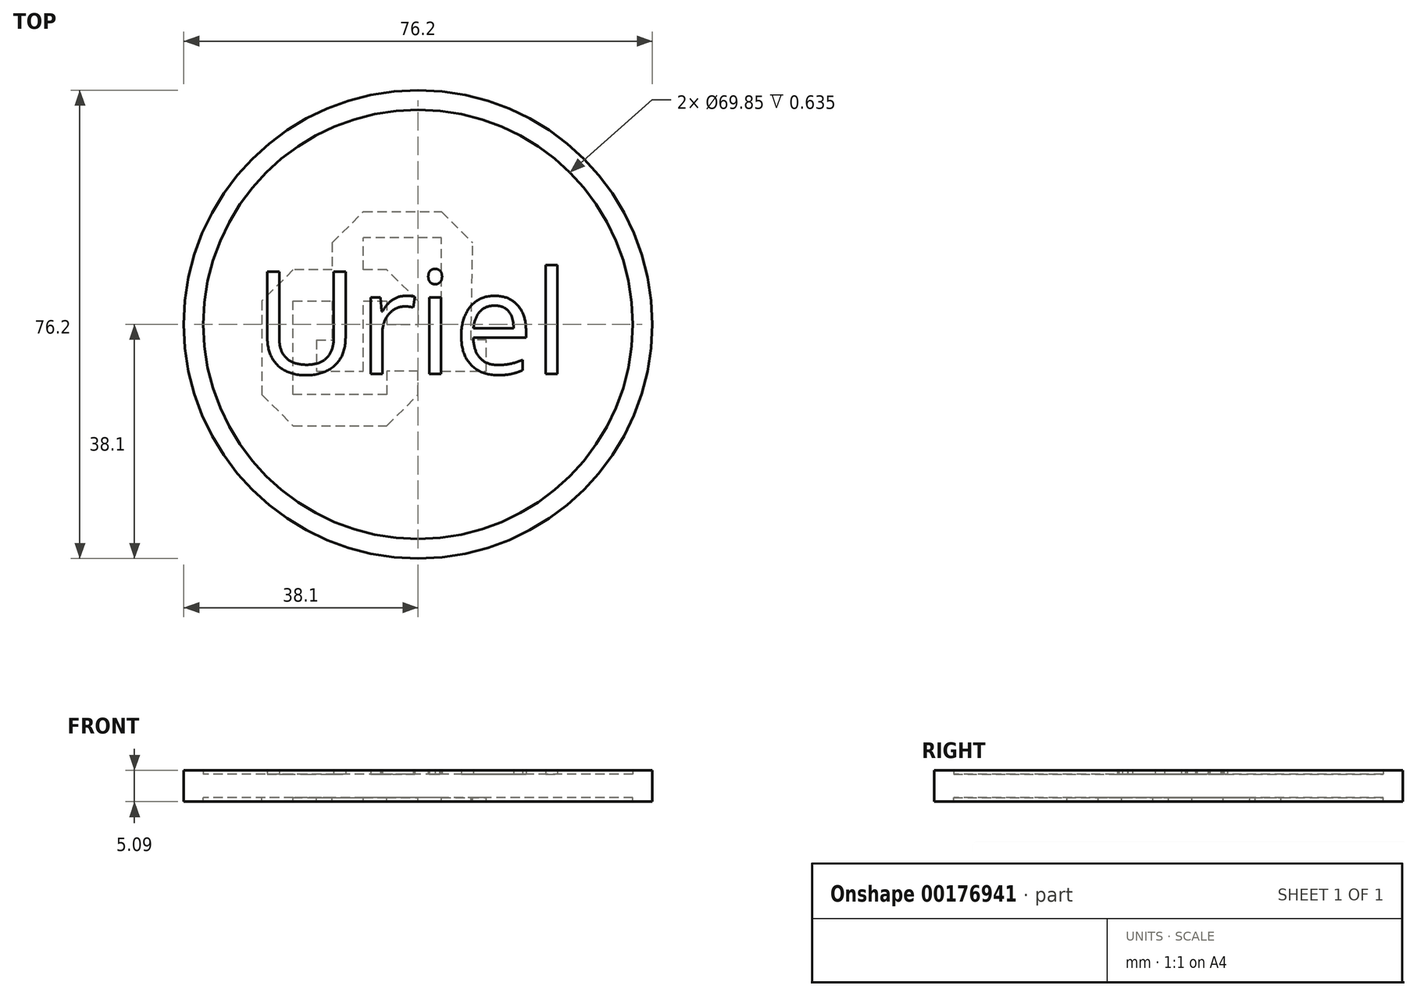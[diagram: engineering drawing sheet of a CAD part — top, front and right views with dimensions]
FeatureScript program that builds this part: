
annotation { "Feature Type Name" : "Feature", "Feature Type Description" : "" }
export const myFeature = defineFeature(function(context is Context, id is Id, definition is map)
    precondition{}
    {
        {
            var Q0;
            Q0=qCreatedBy(makeId("Top.planeOp"),FACE);
            var sketch = newSketch(context, id + "F0", { "sketchPlane" : qUnion([Q0])});
            skCircle(sketch, "E0", {"center": v(0, 0) * mm, "radius": 38.1 * mm});
            skSolve(sketch);
        }
        {
            var Q0;
            Q0 = qSketchRegion(id + "F0", true);
            extrude(context, id + "F1", {"entities" : qUnion([Q0]), "depth" : 3.8 * mm});
        }
        {
            var Q0;
            Q0=qCreatedBy(makeId("Top.planeOp"),FACE);
            var sketch = newSketch(context, id + "F2", { "sketchPlane" : qUnion([Q0])});
            skLineSegment(sketch, "E1", {"start": v(0, 3.8) * mm, "end": v(0, 0) * mm});
            skLineSegment(sketch, "E2", {"start": v(0, 3.8) * mm, "end": v(-5.08, 8.89) * mm});
            skLineSegment(sketch, "E3", {"start": v(-5.08, 8.89) * mm, "end": v(-20.32, 8.89) * mm});
            skLineSegment(sketch, "E4", {"start": v(-20.32, 8.89) * mm, "end": v(-25.4, 3.8) * mm});
            skLineSegment(sketch, "E5", {"start": v(-25.4, 3.8) * mm, "end": v(-25.4, -11.43) * mm});
            skLineSegment(sketch, "E6", {"start": v(-25.4, -11.43) * mm, "end": v(-20.32, -16.51) * mm});
            skLineSegment(sketch, "E7", {"start": v(-20.32, -16.51) * mm, "end": v(-5.08, -16.51) * mm});
            skLineSegment(sketch, "E8", {"start": v(-5.08, -16.51) * mm, "end": v(0, -11.43) * mm});
            skLineSegment(sketch, "E9", {"start": v(0, -11.43) * mm, "end": v(0, -7.62) * mm});
            skLineSegment(sketch, "E10", {"start": v(0, -7.62) * mm, "end": v(-5.08, -7.62) * mm});
            skLineSegment(sketch, "E11", {"start": v(-5.08, -7.62) * mm, "end": v(-5.08, -11.43) * mm});
            skLineSegment(sketch, "E12", {"start": v(-5.08, -11.43) * mm, "end": v(-20.32, -11.43) * mm});
            skLineSegment(sketch, "E13", {"start": v(-20.32, -11.43) * mm, "end": v(-20.32, 3.8) * mm});
            skLineSegment(sketch, "E14", {"start": v(-20.32, 3.8) * mm, "end": v(-5.08, 3.8) * mm});
            skLineSegment(sketch, "E15", {"start": v(-5.08, 3.8) * mm, "end": v(-5.08, 0) * mm});
            skLineSegment(sketch, "E16", {"start": v(-5.08, 0) * mm, "end": v(0, 0) * mm});
            skLineSegment(sketch, "E17", {"start": v(-13.97, 3.8) * mm, "end": v(-13.97, -2.54) * mm});
            skLineSegment(sketch, "E18", {"start": v(-16.5, -2.54) * mm, "end": v(-16.5, -7.62) * mm});
            skLineSegment(sketch, "E19", {"start": v(-13.97, 13.26) * mm, "end": v(-13.97, 3.8) * mm});
            skLineSegment(sketch, "E20", {"start": v(-13.97, 13.26) * mm, "end": v(-8.9, 18.34) * mm});
            skLineSegment(sketch, "E21", {"start": v(-8.9, 18.34) * mm, "end": v(3.8, 18.34) * mm});
            skPoint(sketch, "E22.endSnap0", {"position": v(-2.54, -7.62) * mm});
            skLineSegment(sketch, "E23", {"start": v(-16.5, -2.54) * mm, "end": v(-13.97, -2.54) * mm});
            skLineSegment(sketch, "E24", {"start": v(-16.5, -7.62) * mm, "end": v(-8.89, -7.62) * mm});
            skLineSegment(sketch, "E25", {"start": v(-8.89, -7.62) * mm, "end": v(-8.9, 14.1) * mm});
            skLineSegment(sketch, "E26", {"start": v(3.8, 14.1) * mm, "end": v(-8.9, 14.1) * mm});
            skLineSegment(sketch, "E27", {"start": v(3.8, 18.34) * mm, "end": v(8.88, 13.26) * mm});
            skLineSegment(sketch, "E28", {"start": v(3.8, -7.62) * mm, "end": v(3.8, 14.1) * mm});
            skLineSegment(sketch, "E29", {"start": v(3.8, -7.62) * mm, "end": v(11.13, -7.62) * mm});
            skLineSegment(sketch, "E30", {"start": v(11.13, -7.62) * mm, "end": v(11.13, -2.54) * mm});
            skPoint(sketch, "E30.endSnap0", {"position": v(-15.24, -2.54) * mm});
            skLineSegment(sketch, "E31", {"start": v(8.59, -2.54) * mm, "end": v(8.88, 13.26) * mm});
            skLineSegment(sketch, "E32", {"start": v(11.13, -2.54) * mm, "end": v(8.59, -2.54) * mm});
            skCircle(sketch, "E33.0", {"center": v(0, 0) * mm, "radius": 38.1 * mm});
            skCircle(sketch, "E34.0", {"center": v(0, 0) * mm, "radius": 34.93 * mm});
            skSolve(sketch);
        }
        {
            var Q0;
            {var subQ0=sQuery(id+"F2.wireOp",EDGE,"E25");var subQ1=sQuery(id+"F2.wireOp",EDGE,"E3");var subQ2=makeQuery(id+"F2.imprint","INTERSECT",VERTEX,{"derivedFrom":[subQ1,subQ0]});Q0=makeQuery(id+"F2.imprint","IMPRINT",FACE,{"disambiguationData":[TD([[makeQuery(id+"F2.imprint","IMPRINT",EDGE,{"disambiguationData":[TD([[subQ2,-1.0]])],"derivedFrom":subQ1}),1.0]])]});}
            var Q1;
            {var subQ1=sQuery(id+"F2.wireOp",EDGE,"E4");Q1=makeQuery(id+"F2.imprint","IMPRINT",FACE,{"disambiguationData":[TD([[makeQuery(id+"F2.imprint","IMPRINT",EDGE,{"derivedFrom":subQ1}),1.0]])]});}
            var Q2;
            {var subQ0=sQuery(id+"F2.wireOp",EDGE,"E17");Q2=makeQuery(id+"F2.imprint","IMPRINT",FACE,{"disambiguationData":[TD([[makeQuery(id+"F2.imprint","IMPRINT",EDGE,{"derivedFrom":subQ0}),1.0]])]});}
            var Q3;
            Q3=makeQuery(id+"F2.imprint","IMPRINT",FACE,{"disambiguationData":[TD([[makeQuery(id+"F2.imprint","IMPRINT",EDGE,{"derivedFrom":sQuery(id+"F2.wireOp",EDGE,"E1")}),-1.0]])]});
            var Q4;
            {var subQ0=sQuery(id+"F2.wireOp",EDGE,"E20");Q4=makeQuery(id+"F2.imprint","IMPRINT",FACE,{"disambiguationData":[TD([[makeQuery(id+"F2.imprint","IMPRINT",EDGE,{"derivedFrom":subQ0}),-1.0]])]});}
            var Q5;
            Q5=makeQuery(id+"F2.imprint","IMPRINT",FACE,{"disambiguationData":[TD([[makeQuery(id+"F2.imprint","IMPRINT",EDGE,{"derivedFrom":sQuery(id+"F2.wireOp",EDGE,"E33.0")}),1.0]])]});
            extrude(context, id + "F3", {"entities" : qUnion([Q0, Q1, Q2, Q3, Q4, Q5]), "operationType" : NewBodyOperationType.ADD, "oppositeDirection" : true, "depth" : 0.64 * mm});
        }
        {
            var Q0;
            Q0=makeQuery(id+"F1.opExtrude","CAP_FACE",FACE,{"disambiguationData":[OSD([sQuery(id+"F0.wireOp",EDGE,"E0")])],"isStart":false});
            var sketch = newSketch(context, id + "F4", { "sketchPlane" : qUnion([Q0])});
            skText(sketch, "E35", { "text": "Uriel ", "fontName": "OpenSans-Regular.ttf"});
            const initialGuessF4  = {"E35": [-0.02663, -0.00805, 1, 0, 0.01676]};
            skSetInitialGuess(sketch, initialGuessF4);
            skSolve(sketch);
        }
        {
            var Q0;
            Q0 = qSketchRegion(id + "F4", true);
            extrude(context, id + "F5", {"entities" : qUnion([Q0]), "operationType" : NewBodyOperationType.ADD, "depth" : 0.64 * mm});
        }
        {
            var Q0;
            {var subQ0=sQuery(id+"F0.wireOp",EDGE,"E0");Q0=makeQuery(id+"F5.boolean.opBoolean","SPLIT",FACE,{"disambiguationData":[TD([makeQuery(id+"F1.opExtrude","SWEPT_FACE",FACE,{"disambiguationData":[OSD([subQ0])]})])],"derivedFrom":makeQuery(id+"F1.opExtrude","CAP_FACE",FACE,{"disambiguationData":[OSD([subQ0])],"isStart":false})});}
            var sketch = newSketch(context, id + "F6", { "sketchPlane" : qUnion([Q0])});
            skCircle(sketch, "E36.0", {"center": v(0, 0) * mm, "radius": 34.93 * mm});
            skSolve(sketch);
        }
        {
            var Q0;
            Q0=makeQuery(id+"F6.imprint","IMPRINT",FACE,{"disambiguationData":[TD([[makeQuery(id+"F6.imprint","IMPRINT",EDGE,{"derivedFrom":sQuery(id+"F6.wireOp",EDGE,"E36.0")}),-1.0]])]});
            extrude(context, id + "F7", {"entities" : qUnion([Q0]), "operationType" : NewBodyOperationType.ADD, "depth" : 0.64 * mm});
        }
    });
